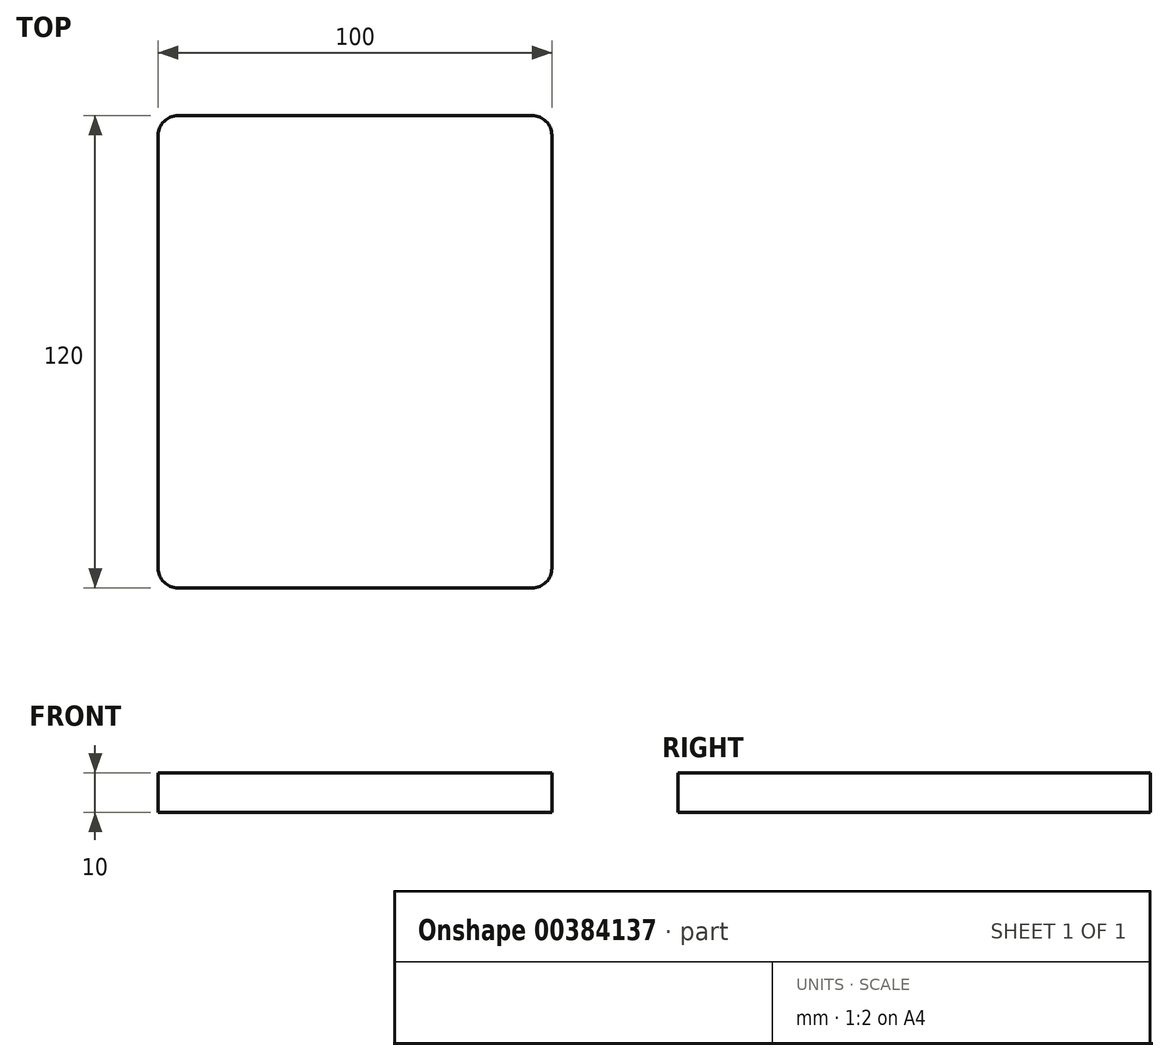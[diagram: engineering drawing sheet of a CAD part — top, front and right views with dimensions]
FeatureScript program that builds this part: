
annotation { "Feature Type Name" : "Feature", "Feature Type Description" : "" }
export const myFeature = defineFeature(function(context is Context, id is Id, definition is map)
    precondition{}
    {
        {
            var Q0;
            Q0=qCreatedBy(makeId("Top.planeOp"),FACE);
            var sketch = newSketch(context, id + "F0", { "sketchPlane" : qUnion([Q0])});
            skLineSegment(sketch, "E0.bottom", {"start": v(45, 60) * mm, "end": v(-45, 60) * mm});
            skLineSegment(sketch, "E0.top", {"start": v(45, -60) * mm, "end": v(-45, -60) * mm});
            skLineSegment(sketch, "E0.left", {"start": v(50, 55) * mm, "end": v(50, -55) * mm});
            skLineSegment(sketch, "E0.right", {"start": v(-50, 55) * mm, "end": v(-50, -55) * mm});
            skPoint(sketch, "E0.middle", {"position": v(0, 0) * mm});
            skPoint(sketch, "E1.visualSharp", {"position": v(-50, 60) * mm});
            skArc(sketch, "E1.filletArc", {"start": v(-45, 60) * mm, "mid": v(-48.54, 58.54) * mm, "end": v(-50, 55) * mm});
            skPoint(sketch, "E2.visualSharp", {"position": v(50, 60) * mm});
            skArc(sketch, "E2.filletArc", {"start": v(50, 55) * mm, "mid": v(48.54, 58.54) * mm, "end": v(45, 60) * mm});
            skPoint(sketch, "E3.visualSharp", {"position": v(50, -60) * mm});
            skArc(sketch, "E3.filletArc", {"start": v(45, -60) * mm, "mid": v(48.54, -58.54) * mm, "end": v(50, -55) * mm});
            skPoint(sketch, "E4.visualSharp", {"position": v(-50, -60) * mm});
            skArc(sketch, "E4.filletArc", {"start": v(-50, -55) * mm, "mid": v(-48.54, -58.54) * mm, "end": v(-45, -60) * mm});
            skSolve(sketch);
        }
        {
            var Q0;
            Q0=makeQuery(id+"F0.imprint","IMPRINT",FACE,{"disambiguationData":[TD([[makeQuery(id+"F0.imprint","IMPRINT",EDGE,{"derivedFrom":sQuery(id+"F0.wireOp",EDGE,"E0.bottom")}),1.0]])]});
            extrude(context, id + "F1", {"entities" : qUnion([Q0]), "depth" : 10 * mm});
        }
    });
